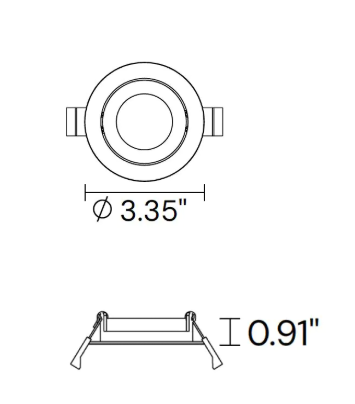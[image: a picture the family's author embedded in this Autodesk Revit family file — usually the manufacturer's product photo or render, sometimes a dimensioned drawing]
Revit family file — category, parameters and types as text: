
# Revit family: Alcon-14078-ADJ-4 -Revit-Family
name_source: partatom
category: Lighting Fixtures
units: mm (PartAtom-declared; Revit-internal decimal feet)

## family parameters
Always vertical = Yes
Cut with Voids When Loaded = No
Host = Ceiling
Light Source = Yes
OmniClass Number = 23.80.70.11
OmniClass Title = Luminaries for Internal Lighting
Part Type = Normal
Room Calculation Point = No
Round Connector Dimension = Use Diameter
Shared = No

## types (1)
- Type 1
    Color Filter = 16777215
    Default Elevation = 0' - 0"
    Dimming Lamp Color Temperature Shift = <None>
    Housing = Default
    Lens = Default
    Light Source Symbol Length = 10' - 0"
    LightSource = light
    Link To Product Page = https://www.alconlighting.com
    Manufacturer = Alcon Light
    Product Identity = Alcon Lighting 14078-ADJ-4
    Spot Beam Angle = 30.00°
    Spot Field Angle = 75.00°
    Tilt Angle = 60.00°

## geometry (parser evidence)
native form markers: Sweep x2
no freeform markers — native parametric forms only
